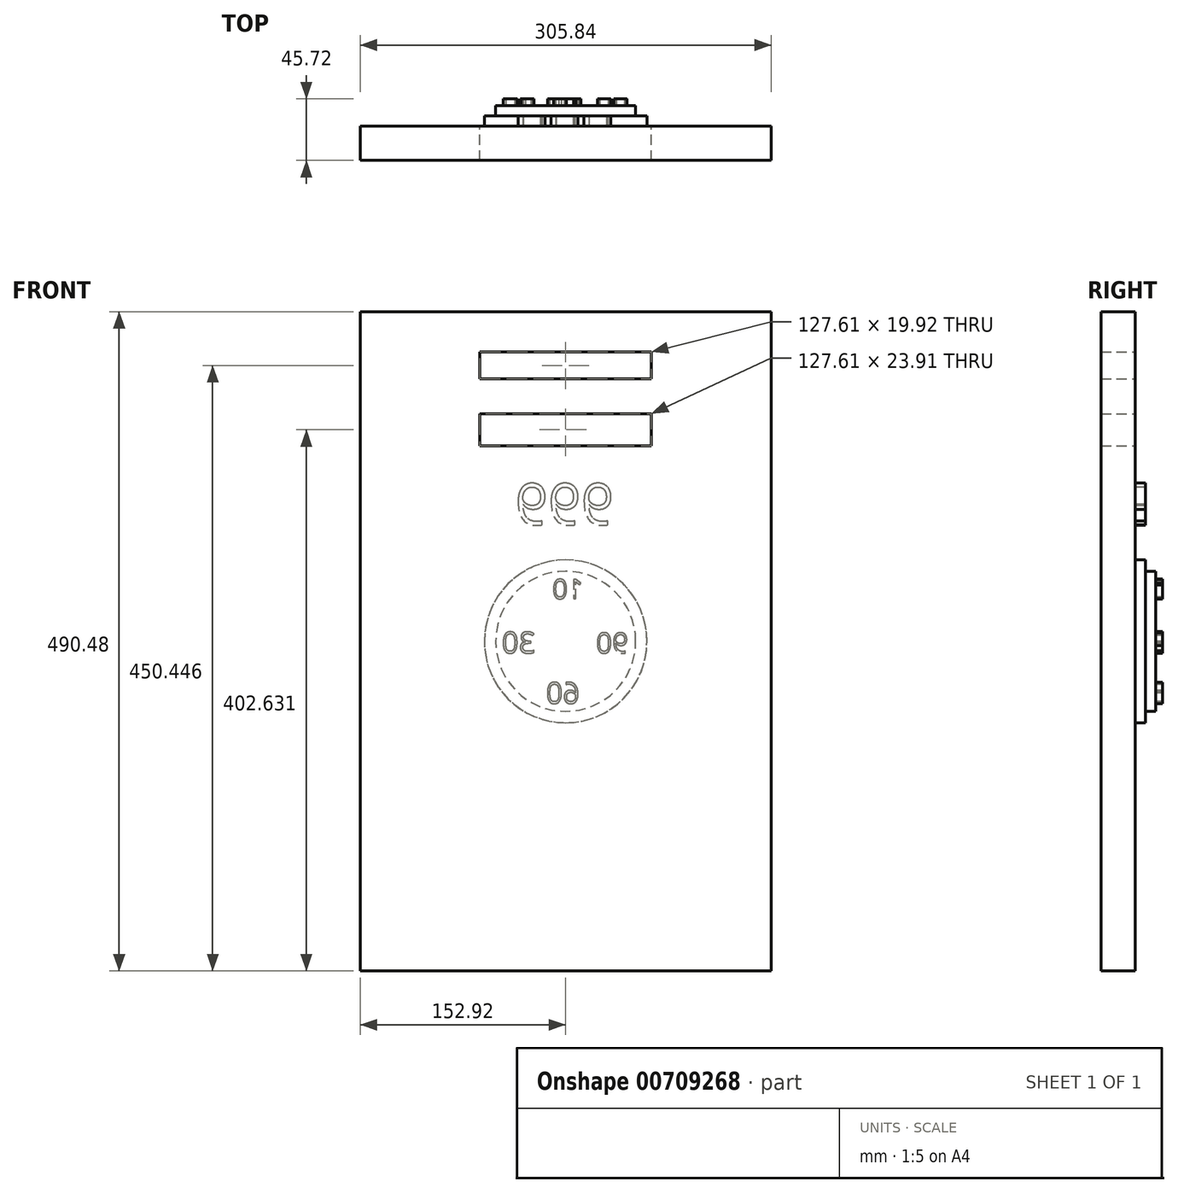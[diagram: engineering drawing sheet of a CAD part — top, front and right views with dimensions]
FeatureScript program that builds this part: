
annotation { "Feature Type Name" : "Feature", "Feature Type Description" : "" }
export const myFeature = defineFeature(function(context is Context, id is Id, definition is map)
    precondition{}
    {
        {
            var Q0;
            Q0=qCreatedBy(makeId("Front.planeOp"),FACE);
            var sketch = newSketch(context, id + "F0", { "sketchPlane" : qUnion([Q0])});
            skLineSegment(sketch, "E0.bottom", {"start": v(152.92, 245.24) * mm, "end": v(-152.92, 245.24) * mm});
            skLineSegment(sketch, "E0.top", {"start": v(152.92, -245.24) * mm, "end": v(-152.92, -245.24) * mm});
            skLineSegment(sketch, "E0.left", {"start": v(152.92, 245.24) * mm, "end": v(152.92, -245.24) * mm});
            skLineSegment(sketch, "E0.right", {"start": v(-152.92, 245.24) * mm, "end": v(-152.92, -245.24) * mm});
            skPoint(sketch, "E0.middle", {"position": v(0, 0) * mm});
            skLineSegment(sketch, "E1.bottom", {"start": v(63.8, 215.17) * mm, "end": v(-63.8, 215.17) * mm});
            skLineSegment(sketch, "E1.top", {"start": v(63.8, 195.24) * mm, "end": v(-63.8, 195.24) * mm});
            skLineSegment(sketch, "E1.left", {"start": v(63.8, 215.17) * mm, "end": v(63.8, 195.24) * mm});
            skLineSegment(sketch, "E1.right", {"start": v(-63.8, 215.17) * mm, "end": v(-63.8, 195.24) * mm});
            skPoint(sketch, "E1.middle", {"position": v(0, 205.2) * mm});
            skLineSegment(sketch, "E2.bottom", {"start": v(63.8, 169.34) * mm, "end": v(-63.8, 169.34) * mm});
            skLineSegment(sketch, "E2.top", {"start": v(63.8, 145.44) * mm, "end": v(-63.8, 145.44) * mm});
            skLineSegment(sketch, "E2.left", {"start": v(63.8, 169.34) * mm, "end": v(63.8, 145.44) * mm});
            skLineSegment(sketch, "E2.right", {"start": v(-63.8, 169.34) * mm, "end": v(-63.8, 145.44) * mm});
            skPoint(sketch, "E2.middle", {"position": v(0, 157.4) * mm});
            skPoint(sketch, "E2.cornerSnap0", {"position": v(63.8, 205.2) * mm});
            skSolve(sketch);
        }
        {
            var Q0;
            Q0=makeQuery(id+"F0.imprint","IMPRINT",FACE,{"disambiguationData":[TD([[makeQuery(id+"F0.imprint","IMPRINT",EDGE,{"derivedFrom":sQuery(id+"F0.wireOp",EDGE,"E0.bottom")}),1.0]])]});
            extrude(context, id + "F1", {"entities" : qUnion([Q0]), "depth" : 25.4 * mm, "offsetDistance" : 25.4 * mm});
        }
        {
            var Q0;
            Q0=makeQuery(id+"F1.opExtrude","CAP_FACE",FACE,{"disambiguationData":[OSD([sQuery(id+"F0.wireOp",EDGE,"E0.bottom"),sQuery(id+"F0.wireOp",EDGE,"E0.top"),sQuery(id+"F0.wireOp",EDGE,"E0.left"),sQuery(id+"F0.wireOp",EDGE,"E0.right"),sQuery(id+"F0.wireOp",EDGE,"E1.bottom"),sQuery(id+"F0.wireOp",EDGE,"E1.top"),sQuery(id+"F0.wireOp",EDGE,"E1.left"),sQuery(id+"F0.wireOp",EDGE,"E1.right"),sQuery(id+"F0.wireOp",EDGE,"E2.bottom"),sQuery(id+"F0.wireOp",EDGE,"E2.top"),sQuery(id+"F0.wireOp",EDGE,"E2.left"),sQuery(id+"F0.wireOp",EDGE,"E2.right")])],"isStart":true});
            var sketch = newSketch(context, id + "F2", { "sketchPlane" : qUnion([Q0])});
            skText(sketch, "E3", { "text": "999", "fontName": "OpenSans-Regular.ttf"});
            const initialGuessF2  = {"E3": [-0.03591, 0.08666, 1, 0, 0.03088]};
            skSetInitialGuess(sketch, initialGuessF2);
            skSolve(sketch);
        }
        {
            var Q0;
            Q0 = qSketchRegion(id + "F2", true);
            extrude(context, id + "F3", {"entities" : qUnion([Q0]), "operationType" : NewBodyOperationType.ADD, "depth" : 7.62 * mm, "offsetDistance" : 25.4 * mm});
        }
        {
            var Q0;
            {var subQ0=sQuery(id+"F0.wireOp",EDGE,"E2.bottom");var subQ1=sQuery(id+"F0.wireOp",EDGE,"E1.right");var subQ2=sQuery(id+"F0.wireOp",EDGE,"E1.left");var subQ3=sQuery(id+"F0.wireOp",EDGE,"E1.top");var subQ4=sQuery(id+"F0.wireOp",EDGE,"E1.bottom");var subQ5=sQuery(id+"F0.wireOp",EDGE,"E2.top");var subQ6=sQuery(id+"F0.wireOp",EDGE,"E0.bottom");var subQ7=sQuery(id+"F0.wireOp",EDGE,"E0.right");var subQ8=sQuery(id+"F0.wireOp",EDGE,"E0.top");var subQ9=sQuery(id+"F0.wireOp",EDGE,"E0.left");var subQ10=sQuery(id+"F0.wireOp",EDGE,"E2.left");var subQ11=sQuery(id+"F0.wireOp",EDGE,"E2.right");Q0=makeQuery(id+"F3.boolean.opBoolean","SPLIT",FACE,{"disambiguationData":[TD([makeQuery(id+"F1.opExtrude","SWEPT_FACE",FACE,{"disambiguationData":[OSD([subQ6])]})])],"derivedFrom":makeQuery(id+"F1.opExtrude","CAP_FACE",FACE,{"disambiguationData":[OSD([subQ6,subQ8,subQ9,subQ7,subQ4,subQ3,subQ2,subQ1,subQ0,subQ5,subQ10,subQ11])],"isStart":true})});}
            var sketch = newSketch(context, id + "F4", { "sketchPlane" : qUnion([Q0])});
            skCircle(sketch, "E4", {"center": v(0, 0) * mm, "radius": 60.53 * mm});
            skSolve(sketch);
        }
        {
            var Q0;
            Q0 = qSketchRegion(id + "F4", true);
            extrude(context, id + "F5", {"entities" : qUnion([Q0]), "operationType" : NewBodyOperationType.ADD, "depth" : 7.62 * mm, "offsetDistance" : 25.4 * mm});
        }
        {
            var Q0;
            Q0=makeQuery(id+"F5.opExtrude","CAP_FACE",FACE,{"disambiguationData":[OSD([sQuery(id+"F4.wireOp",EDGE,"E4")])],"isStart":false});
            var sketch = newSketch(context, id + "F6", { "sketchPlane" : qUnion([Q0])});
            skCircle(sketch, "E5", {"center": v(0, 0) * mm, "radius": 52.1 * mm});
            skSolve(sketch);
        }
        {
            var Q0;
            Q0 = qSketchRegion(id + "F6", true);
            extrude(context, id + "F7", {"entities" : qUnion([Q0]), "operationType" : NewBodyOperationType.ADD, "depth" : 7.62 * mm, "offsetDistance" : 25.4 * mm});
        }
        {
            var Q0;
            Q0=makeQuery(id+"F7.opExtrude","CAP_FACE",FACE,{"disambiguationData":[OSD([sQuery(id+"F6.wireOp",EDGE,"E5")])],"isStart":false});
            var sketch = newSketch(context, id + "F8", { "sketchPlane" : qUnion([Q0])});
            skText(sketch, "E6", { "text": "10", "fontName": "OpenSans-Regular.ttf"});
            skText(sketch, "E7", { "text": "30", "fontName": "OpenSans-Regular.ttf"});
            skText(sketch, "E8", { "text": "60", "fontName": "OpenSans-Regular.ttf"});
            skText(sketch, "E9", { "text": "90", "fontName": "OpenSans-Regular.ttf"});
            const initialGuessF8  = {"E6": [-0.01303, 0.03169, 1, 0, 0.01447], "E7": [0.02248, -0.00875, 1, 0, 0.01578], "E8": [-0.0104, -0.04623, 1, 0, 0.01578], "E9": [-0.04657, -0.00875, 1, 0, 0.01512]};
            skSetInitialGuess(sketch, initialGuessF8);
            skSolve(sketch);
        }
        {
            var Q0;
            Q0 = qSketchRegion(id + "F8", true);
            extrude(context, id + "F9", {"entities" : qUnion([Q0]), "operationType" : NewBodyOperationType.ADD, "depth" : 5.08 * mm, "offsetDistance" : 25.4 * mm});
        }
    });
